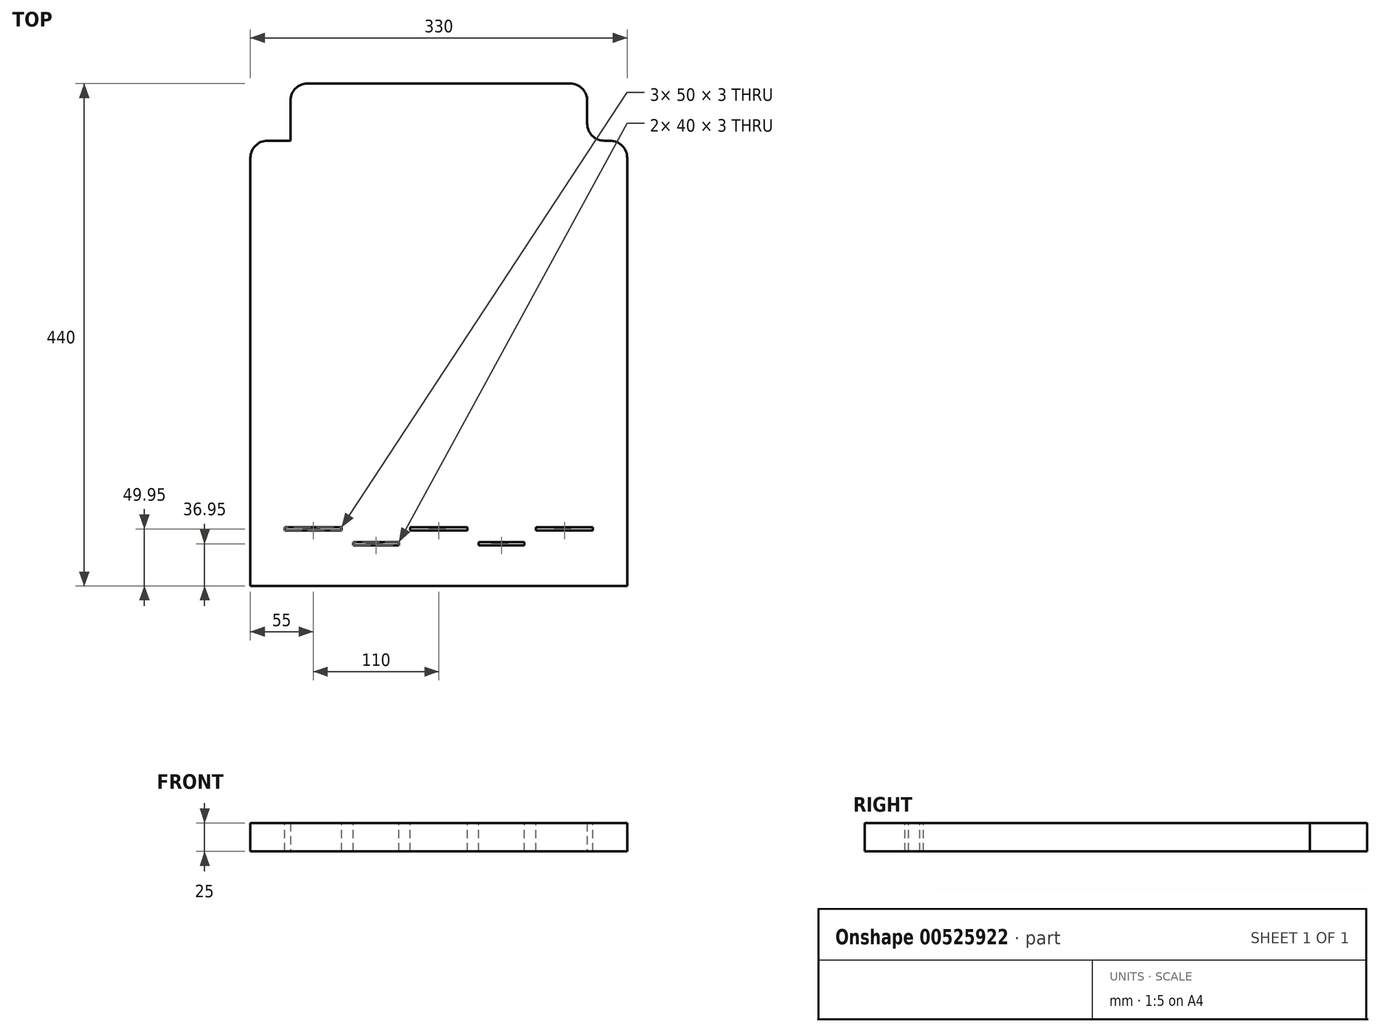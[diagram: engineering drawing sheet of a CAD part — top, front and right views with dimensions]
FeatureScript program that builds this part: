
annotation { "Feature Type Name" : "Feature", "Feature Type Description" : "" }
export const myFeature = defineFeature(function(context is Context, id is Id, definition is map)
    precondition{}
    {
        {
            var Q0;
            Q0=qCreatedBy(makeId("Top.planeOp"),FACE);
            var sketch = newSketch(context, id + "F0", { "sketchPlane" : qUnion([Q0])});
            skLineSegment(sketch, "E0.bottom", {"start": v(145, -175) * mm, "end": v(-145, -175) * mm, "construction": true});
            skLineSegment(sketch, "E0.top", {"start": v(145, 175) * mm, "end": v(-145, 175) * mm, "construction": true});
            skLineSegment(sketch, "E0.left", {"start": v(145, -175) * mm, "end": v(145, 175) * mm, "construction": true});
            skLineSegment(sketch, "E0.right", {"start": v(-145, -175) * mm, "end": v(-145, 175) * mm, "construction": true});
            skPoint(sketch, "E0.middle", {"position": v(0, 0) * mm});
            skLineSegment(sketch, "E1.bottom", {"start": v(165, -195) * mm, "end": v(-165, -195) * mm});
            skLineSegment(sketch, "E1.top", {"start": v(165, 195) * mm, "end": v(-165, 195) * mm});
            skLineSegment(sketch, "E1.left", {"start": v(165, -195) * mm, "end": v(165, 195) * mm});
            skLineSegment(sketch, "E1.right", {"start": v(-165, -195) * mm, "end": v(-165, 195) * mm});
            skSolve(sketch);
        }
        {
            var Q0;
            Q0 = qSketchRegion(id + "F0", true);
            extrude(context, id + "F1", {"entities" : qUnion([Q0]), "depth" : 25 * mm, "offsetDistance" : 25 * mm});
        }
        {
            var Q0;
            Q0=makeQuery(id+"F1.opExtrude","SWEPT_FACE",FACE,{"disambiguationData":[OSD([sQuery(id+"F0.wireOp",EDGE,"E1.top")])]});
            var sketch = newSketch(context, id + "F2", { "sketchPlane" : qUnion([Q0])});
            skLineSegment(sketch, "E2.bottom", {"start": v(-130, 25) * mm, "end": v(130, 25) * mm});
            skLineSegment(sketch, "E2.top", {"start": v(-130, 0) * mm, "end": v(130, 0) * mm});
            skLineSegment(sketch, "E2.left", {"start": v(-130, 25) * mm, "end": v(-130, 0) * mm});
            skLineSegment(sketch, "E2.right", {"start": v(130, 25) * mm, "end": v(130, 0) * mm});
            skSolve(sketch);
        }
        {
            var Q0;
            Q0 = qSketchRegion(id + "F2", true);
            extrude(context, id + "F3", {"entities" : qUnion([Q0]), "operationType" : NewBodyOperationType.ADD, "depth" : 50 * mm, "offsetDistance" : 25 * mm});
        }
        {
            var Q0;
            Q0=makeQuery(id+"F1.opExtrude","SWEPT_EDGE",EDGE,{"disambiguationData":[OSD([sQuery(id+"F0.wireOp",EDGE,"E1.top"),sQuery(id+"F0.wireOp",EDGE,"E1.right")])]});
            var Q1;
            Q1=makeQuery(id+"F3.opExtrude","CAP_EDGE",EDGE,{"disambiguationData":[OSD([sQuery(id+"F2.wireOp",EDGE,"E2.right")])],"isStart":false});
            var Q2;
            Q2=makeQuery(id+"F3.opExtrude","CAP_EDGE",EDGE,{"disambiguationData":[OSD([sQuery(id+"F2.wireOp",EDGE,"E2.left")])],"isStart":false});
            var Q3;
            Q3=makeQuery(id+"F1.opExtrude","SWEPT_EDGE",EDGE,{"disambiguationData":[OSD([sQuery(id+"F0.wireOp",EDGE,"E1.top"),sQuery(id+"F0.wireOp",EDGE,"E1.left")])]});
            var Q4;
            Q4=makeQuery(id+"F3.opExtrude","CAP_EDGE",EDGE,{"disambiguationData":[OSD([sQuery(id+"F2.wireOp",EDGE,"E2.right")])],"isStart":true});
            var Q5;
            Q5=makeQuery(id+"F3.opExtrude","CAP_EDGE",EDGE,{"disambiguationData":[OSD([sQuery(id+"F2.wireOp",EDGE,"E2.left")])],"isStart":true});
            fillet(context, id + "F4", {"entities" : qUnion([Q0, Q1, Q2, Q3, Q4, Q5]), "radius" : 15 * mm, "tangentPropagation" : true, "allowEdgeOverflow" : false});
        }
        {
            var Q0;
            Q0=makeQuery(id+"F3.boolean.opBoolean","MERGE",FACE,{"derivedFrom":[makeQuery(id+"F1.opExtrude","CAP_FACE",FACE,{"disambiguationData":[OSD([sQuery(id+"F0.wireOp",EDGE,"E1.bottom"),sQuery(id+"F0.wireOp",EDGE,"E1.top"),sQuery(id+"F0.wireOp",EDGE,"E1.left"),sQuery(id+"F0.wireOp",EDGE,"E1.right")])],"isStart":false}),makeQuery(id+"F3.opExtrude","SWEPT_FACE",FACE,{"disambiguationData":[OSD([sQuery(id+"F2.wireOp",EDGE,"E2.bottom")])]})]});
            var sketch = newSketch(context, id + "F5", { "sketchPlane" : qUnion([Q0])});
            skLineSegment(sketch, "E3.bottom", {"start": v(-135, -143.55) * mm, "end": v(-85, -143.55) * mm});
            skLineSegment(sketch, "E3.top", {"start": v(-135, -146.55) * mm, "end": v(-85, -146.55) * mm});
            skLineSegment(sketch, "E3.left", {"start": v(-135, -143.55) * mm, "end": v(-135, -146.55) * mm});
            skLineSegment(sketch, "E3.right", {"start": v(-85, -143.55) * mm, "end": v(-85, -146.55) * mm});
            skLineSegment(sketch, "E4.bottom", {"start": v(-25, -146.55) * mm, "end": v(25, -146.55) * mm});
            skLineSegment(sketch, "E4.top", {"start": v(-25, -143.55) * mm, "end": v(25, -143.55) * mm});
            skLineSegment(sketch, "E4.left", {"start": v(-25, -146.55) * mm, "end": v(-25, -143.55) * mm});
            skLineSegment(sketch, "E4.right", {"start": v(25, -146.55) * mm, "end": v(25, -143.55) * mm});
            skLineSegment(sketch, "E5.bottom", {"start": v(85, -146.55) * mm, "end": v(135, -146.55) * mm});
            skLineSegment(sketch, "E5.top", {"start": v(85, -143.55) * mm, "end": v(135, -143.55) * mm});
            skLineSegment(sketch, "E5.left", {"start": v(85, -146.55) * mm, "end": v(85, -143.55) * mm});
            skLineSegment(sketch, "E5.right", {"start": v(135, -146.55) * mm, "end": v(135, -143.55) * mm});
            skLineSegment(sketch, "E6.bottom", {"start": v(-75, -156.55) * mm, "end": v(-35, -156.55) * mm});
            skLineSegment(sketch, "E6.top", {"start": v(-75, -159.55) * mm, "end": v(-35, -159.55) * mm});
            skLineSegment(sketch, "E6.left", {"start": v(-75, -156.55) * mm, "end": v(-75, -159.55) * mm});
            skLineSegment(sketch, "E6.right", {"start": v(-35, -156.55) * mm, "end": v(-35, -159.55) * mm});
            skLineSegment(sketch, "E7.bottom", {"start": v(35, -159.55) * mm, "end": v(75, -159.55) * mm});
            skLineSegment(sketch, "E7.top", {"start": v(35, -156.55) * mm, "end": v(75, -156.55) * mm});
            skLineSegment(sketch, "E7.left", {"start": v(35, -159.55) * mm, "end": v(35, -156.55) * mm});
            skLineSegment(sketch, "E7.right", {"start": v(75, -159.55) * mm, "end": v(75, -156.55) * mm});
            skSolve(sketch);
        }
        {
            var Q0;
            Q0 = qSketchRegion(id + "F5", true);
            extrude(context, id + "F6", {"entities" : qUnion([Q0]), "operationType" : NewBodyOperationType.REMOVE, "oppositeDirection" : true, "depth" : 25 * mm, "offsetDistance" : 25 * mm});
        }
    });
